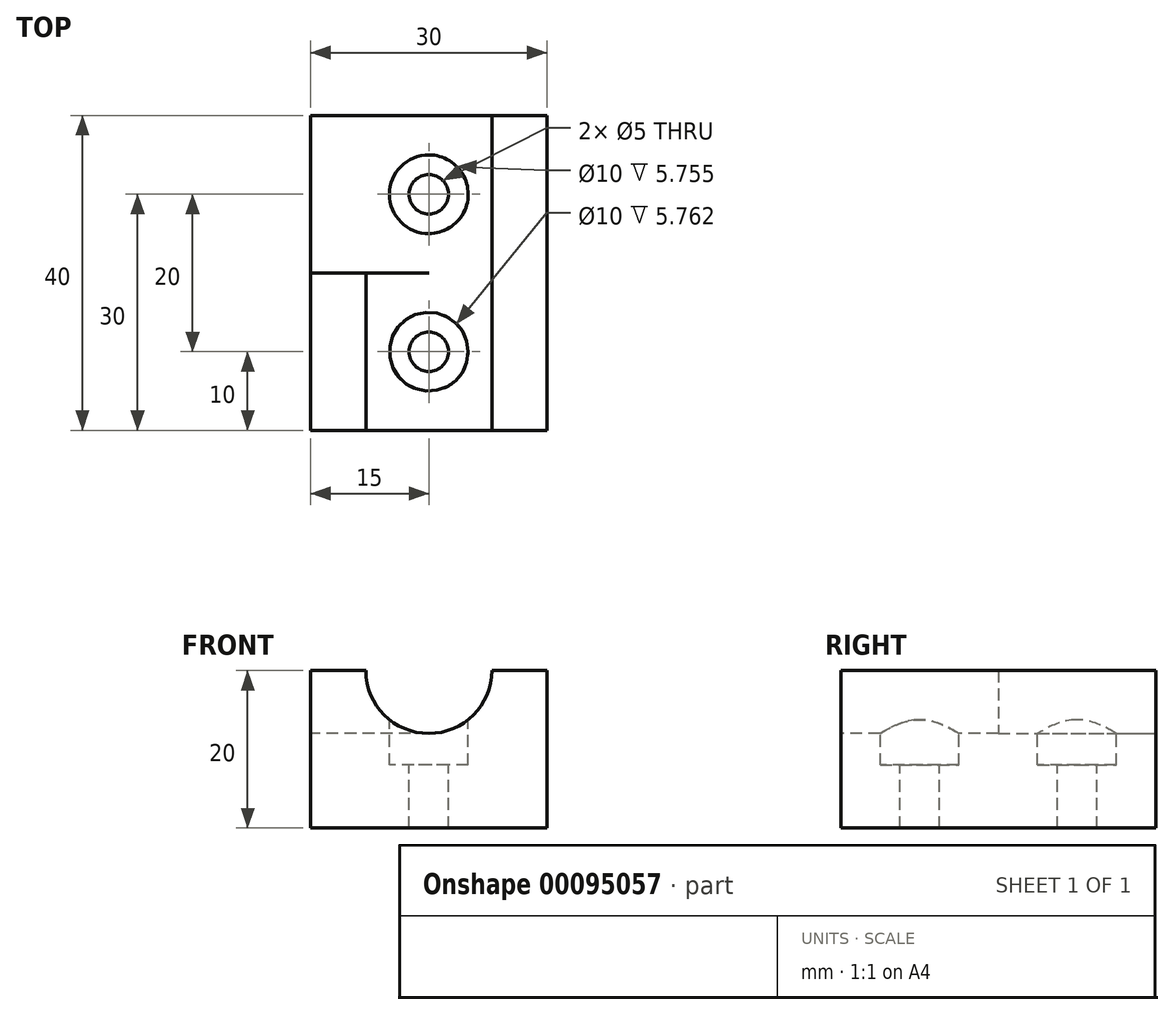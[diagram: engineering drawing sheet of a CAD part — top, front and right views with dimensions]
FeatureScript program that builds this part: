
annotation { "Feature Type Name" : "Feature", "Feature Type Description" : "" }
export const myFeature = defineFeature(function(context is Context, id is Id, definition is map)
    precondition{}
    {
        {
            var Q0;
            Q0=qCreatedBy(makeId("Top.planeOp"),FACE);
            var sketch = newSketch(context, id + "F0", { "sketchPlane" : qUnion([Q0])});
            skLineSegment(sketch, "E0.bottom", {"start": v(15, -20) * mm, "end": v(-15, -20) * mm});
            skLineSegment(sketch, "E0.top", {"start": v(15, 20) * mm, "end": v(-15, 20) * mm});
            skLineSegment(sketch, "E0.left", {"start": v(15, -20) * mm, "end": v(15, 20) * mm});
            skLineSegment(sketch, "E0.right", {"start": v(-15, -20) * mm, "end": v(-15, 20) * mm});
            skPoint(sketch, "E0.middle", {"position": v(0, 0) * mm});
            skSolve(sketch);
        }
        {
            var Q0;
            Q0=makeQuery(id+"F0.imprint","IMPRINT",FACE,{"disambiguationData":[TD([[makeQuery(id+"F0.imprint","IMPRINT",EDGE,{"derivedFrom":sQuery(id+"F0.wireOp",EDGE,"E0.bottom")}),-1.0]])]});
            extrude(context, id + "F1", {"entities" : qUnion([Q0]), "depth" : 20 * mm});
        }
        {
            var Q0;
            Q0=makeQuery(id+"F1.opExtrude","SWEPT_FACE",FACE,{"disambiguationData":[OSD([sQuery(id+"F0.wireOp",EDGE,"E0.bottom")])]});
            var sketch = newSketch(context, id + "F6", { "sketchPlane" : qUnion([Q0])});
            skCircle(sketch, "E1", {"center": v(0, 20) * mm, "radius": 8 * mm});
            skSolve(sketch);
        }
        {
            var Q0;
            Q0=makeQuery(id+"F1.opExtrude","CAP_FACE",FACE,{"disambiguationData":[OSD([sQuery(id+"F0.wireOp",EDGE,"E0.bottom"),sQuery(id+"F0.wireOp",EDGE,"E0.top"),sQuery(id+"F0.wireOp",EDGE,"E0.left"),sQuery(id+"F0.wireOp",EDGE,"E0.right")])],"isStart":false});
            var sketch = newSketch(context, id + "F2", { "sketchPlane" : qUnion([Q0])});
            skPoint(sketch, "E2", {"position": v(0, -10) * mm});
            skPoint(sketch, "E3", {"position": v(0, 10) * mm});
            skSolve(sketch);
        }
        {
            var Q0;
            Q0=sQuery(id+"F2.wireOp",VERTEX,"E2");
            var Q1;
            Q1=sQuery(id+"F2.wireOp",VERTEX,"E3");
            var Q2;
            Q2=makeQuery(id+"F1.opExtrude","SWEPT_BODY",BODY,{"disambiguationData":[OSD([sQuery(id+"F0.wireOp",EDGE,"E0.bottom"),sQuery(id+"F0.wireOp",EDGE,"E0.top"),sQuery(id+"F0.wireOp",EDGE,"E0.left"),sQuery(id+"F0.wireOp",EDGE,"E0.right")])]});
            hole(context, id + "F7", {"style" : HoleStyle.C_BORE, "endStyle" : HoleEndStyle.THROUGH, "holeDiameter" : 5 * mm, "cBoreDiameter" : 10 * mm, "cBoreDepth" : 12 * mm, "locations" : qUnion([Q0, Q1]), "scope" : qUnion([Q2]), "isTappedThrough" : true});
        }
        {
            var Q0;
            {var subQ0=sQuery(id+"F6.wireOp",EDGE,"E1");var subQ1=makeQuery(id+"F1.opExtrude","CAP_EDGE",EDGE,{"disambiguationData":[OSD([sQuery(id+"F0.wireOp",EDGE,"E0.bottom")])],"isStart":false});var subQ2=makeQuery(id+"F6.imprint","INTERSECT",VERTEX,{"disambiguationData":[OD(0.0)],"derivedFrom":[subQ1,subQ0]});Q0=makeQuery(id+"F6.imprint","IMPRINT",FACE,{"disambiguationData":[TD([[makeQuery(id+"F6.imprint","IMPRINT",EDGE,{"disambiguationData":[TD([[subQ2,1.0]])],"derivedFrom":subQ0}),1.0]])]});}
            var Q1;
            {var subQ0=sQuery(id+"F6.wireOp",EDGE,"E1");var subQ1=makeQuery(id+"F1.opExtrude","CAP_EDGE",EDGE,{"disambiguationData":[OSD([sQuery(id+"F0.wireOp",EDGE,"E0.bottom")])],"isStart":false});var subQ2=makeQuery(id+"F6.imprint","INTERSECT",VERTEX,{"disambiguationData":[OD(0.0)],"derivedFrom":[subQ1,subQ0]});Q1=makeQuery(id+"F6.imprint","IMPRINT",FACE,{"disambiguationData":[TD([[makeQuery(id+"F6.imprint","IMPRINT",EDGE,{"disambiguationData":[TD([[subQ2,-1.0]])],"derivedFrom":subQ0}),1.0]])]});}
            extrude(context, id + "F8", {"entities" : qUnion([Q0, Q1]), "operationType" : NewBodyOperationType.REMOVE, "oppositeDirection" : true, "depth" : 40 * mm});
        }
        {
            var Q0;
            Q0=makeQuery(id+"F1.opExtrude","SWEPT_FACE",FACE,{"disambiguationData":[OSD([sQuery(id+"F0.wireOp",EDGE,"E0.top")])]});
            var sketch = newSketch(context, id + "F3", { "sketchPlane" : qUnion([Q0])});
            skLineSegment(sketch, "E4", {"start": v(0, 12) * mm, "end": v(-15, 12) * mm});
            skLineSegment(sketch, "E5", {"start": v(-15, 12) * mm, "end": v(15, 12) * mm});
            skSolve(sketch);
        }
        {
            var Q0;
            {var subQ0=sQuery(id+"F3.wireOp",EDGE,"E5");var subQ5=sQuery(id+"F6.wireOp",EDGE,"E1");var subQ6=makeQuery(id+"F8.boolean.opBoolean","COPY",EDGE,{"derivedFrom":makeQuery(id+"F8.opExtrude","CAP_EDGE",EDGE,{"disambiguationData":[OSD([subQ5])],"isStart":false})});var subQ7=makeQuery(id+"F3.imprint","INTERSECT",VERTEX,{"derivedFrom":[subQ6,subQ0]});Q0=makeQuery(id+"F3.imprint","IMPRINT",FACE,{"disambiguationData":[TD([[makeQuery(id+"F3.imprint","IMPRINT",EDGE,{"disambiguationData":[TD([[subQ7,1.0]])],"derivedFrom":subQ0}),1.0]])]});}
            var Q1;
            {var subQ0=sQuery(id+"F3.wireOp",EDGE,"E5");var subQ5=sQuery(id+"F6.wireOp",EDGE,"E1");var subQ6=makeQuery(id+"F8.boolean.opBoolean","COPY",EDGE,{"derivedFrom":makeQuery(id+"F8.opExtrude","CAP_EDGE",EDGE,{"disambiguationData":[OSD([subQ5])],"isStart":false})});var subQ7=makeQuery(id+"F3.imprint","INTERSECT",VERTEX,{"derivedFrom":[subQ6,subQ0]});Q1=makeQuery(id+"F3.imprint","IMPRINT",FACE,{"disambiguationData":[TD([[makeQuery(id+"F3.imprint","IMPRINT",EDGE,{"disambiguationData":[TD([[subQ7,-1.0]])],"derivedFrom":subQ0}),1.0]])]});}
            extrude(context, id + "F4", {"entities" : qUnion([Q0, Q1]), "operationType" : NewBodyOperationType.REMOVE, "oppositeDirection" : true, "depth" : 20 * mm});
        }
    });
